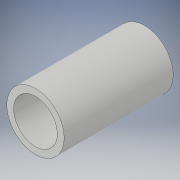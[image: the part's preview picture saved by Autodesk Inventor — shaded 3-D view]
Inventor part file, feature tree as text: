
AUTODESK INVENTOR PART (.ipt)
format: ipt  version: 2018 (Build 220112000, 112)  size: 97,792 bytes
history: native  units: in
note: dims shown in document units (in); Inventor stores cm internally (conversion verified against a paired STEP export)
features: extrude x1, sketch x1
ambient origin geometry x8: Origin, YZ Plane, XZ Plane, XY Plane, X Axis, Y Axis, Z Axis, Center Point
bodies: Solid1 (feature_tree)
feature tree (2):
  extrude  "Extrusion1"  Depth=2.5in
  sketch  "Sketch1"  dims[d0=1.315in d1=1.0in d2=2.5in d3=0.0in]
